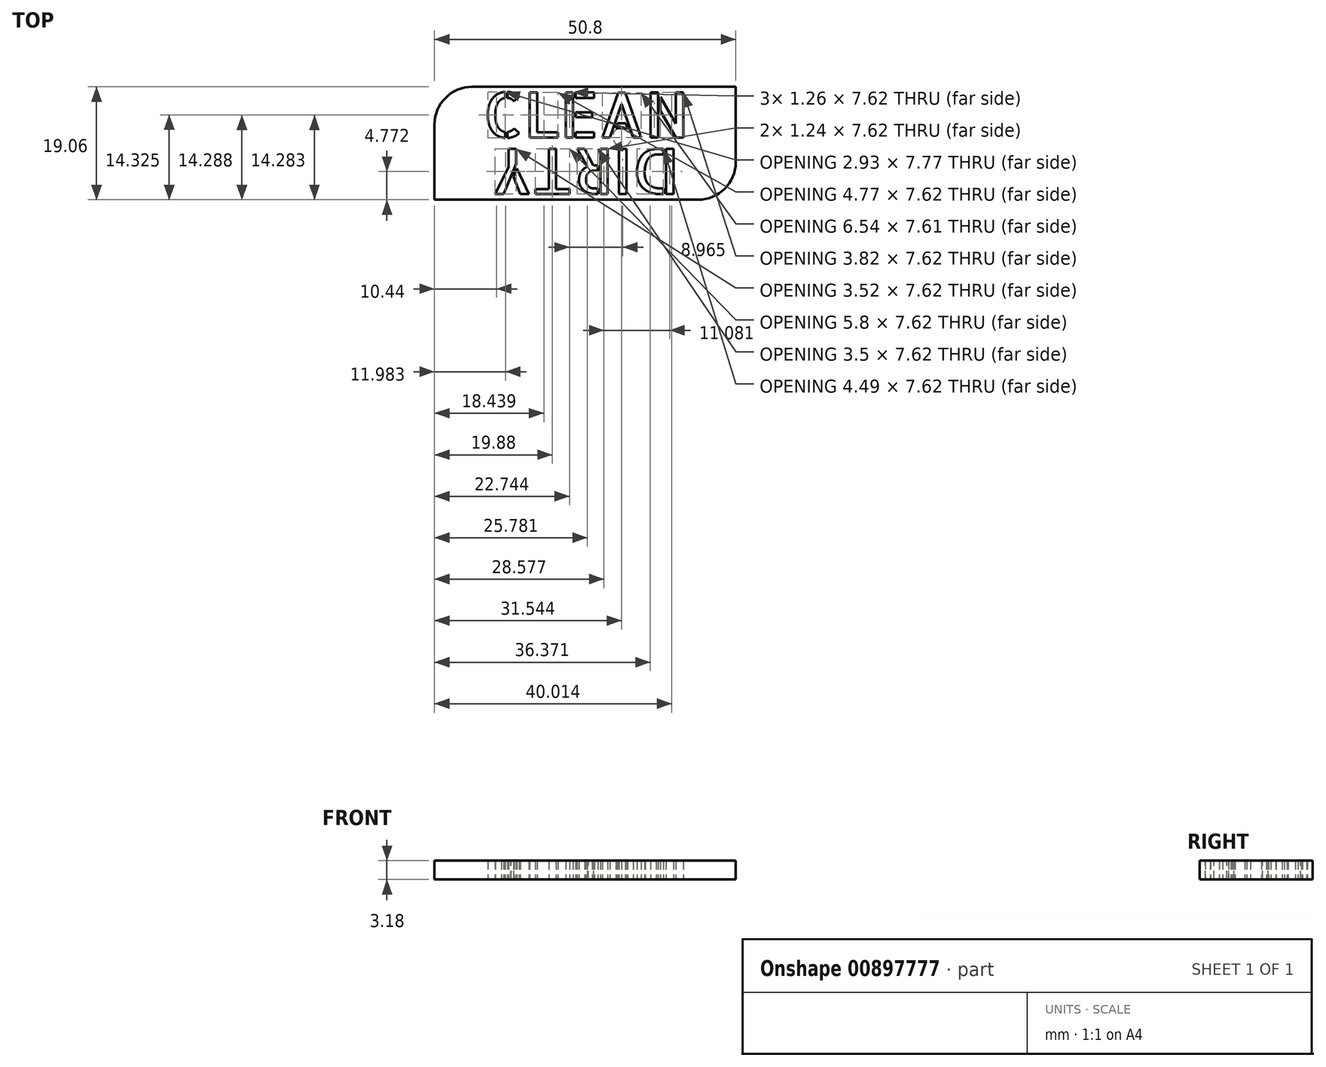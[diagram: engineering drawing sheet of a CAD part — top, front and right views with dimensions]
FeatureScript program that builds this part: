
annotation { "Feature Type Name" : "Feature", "Feature Type Description" : "" }
export const myFeature = defineFeature(function(context is Context, id is Id, definition is map)
    precondition{}
    {
        {
            assignVariable(context, id + "F0", {"name" : "MagnetHeight", "anyValue" : 0.06});
        }
        {
            var Q0;
            Q0=qCreatedBy(makeId("Top.planeOp"),FACE);
            var sketch = newSketch(context, id + "F1", { "sketchPlane" : qUnion([Q0])});
            skLineSegment(sketch, "E0.bottom", {"start": v(-36.28, 9.53) * mm, "end": v(8.17, 9.52) * mm});
            skLineSegment(sketch, "E0.top", {"start": v(-42.63, -9.52) * mm, "end": v(1.82, -9.53) * mm});
            skLineSegment(sketch, "E0.left", {"start": v(-42.63, 3.18) * mm, "end": v(-42.63, -9.52) * mm});
            skLineSegment(sketch, "E0.right", {"start": v(8.17, 9.52) * mm, "end": v(8.17, -3.18) * mm});
            skLineSegment(sketch, "E1", {"start": v(-42.63, 0) * mm, "end": v(8.17, 0) * mm, "construction": true});
            skText(sketch, "E2", { "text": "DIRTY", "fontName": "AllertaStencil-Regular.ttf"});
            skPoint(sketch, "E3.visualSharp", {"position": v(-42.63, 9.52) * mm});
            skArc(sketch, "E3.filletArc", {"start": v(-36.28, 9.53) * mm, "mid": v(-40.77, 7.67) * mm, "end": v(-42.63, 3.18) * mm});
            skPoint(sketch, "E4.visualSharp", {"position": v(8.17, -9.52) * mm});
            skArc(sketch, "E4.filletArc", {"start": v(1.82, -9.53) * mm, "mid": v(6.3, -7.67) * mm, "end": v(8.17, -3.18) * mm});
            skText(sketch, "E5", { "text": "CLEAN", "fontName": "AllertaStencil-Regular.ttf"});
            const initialGuessF1  = {"E2": [-0.00136, -0.00095, -1, 0, 0.00762], "E5": [-0.03447, 0.00095, 1, 0, 0.00762]};
            skSetInitialGuess(sketch, initialGuessF1);
            skSolve(sketch);
        }
        {
            var Q0;
            Q0=makeQuery(id+"F1.imprint","IMPRINT",FACE,{"disambiguationData":[TD([[makeQuery(id+"F1.imprint","IMPRINT",EDGE,{"derivedFrom":sQuery(id+"F1.wireOp",EDGE,"E0.bottom")}),-1.0]])]});
            extrude(context, id + "F2", {"entities" : qUnion([Q0]), "depth" : 3.17 * mm, "offsetDistance" : 25.4 * mm});
        }
        {
            var Q0;
            Q0=makeQuery(id+"F1.imprint","IMPRINT",FACE,{"disambiguationData":[TD([[makeQuery(id+"F1.imprint","IMPRINT",EDGE,{"derivedFrom":sQuery(id+"F1.wireOp",EDGE,"E5.sketch_text.stroke-41")}),1.0]])]});
            var sketch = newSketch(context, id + "F3", { "sketchPlane" : qUnion([Q0])});
            skCircle(sketch, "E6", {"center": v(-10.98, 1.1) * mm, "radius": 1.59 * mm});
            skSolve(sketch);
        }
        {
            var Q0;
            Q0 = qSketchRegion(id + "F3", true);
            extrude(context, id + "F4", {"entities" : qUnion([Q0]), "operationType" : NewBodyOperationType.REMOVE, "oppositeDirection" : true, "depth" : -(getVariable(context, 'MagnetHeight')) * mm, "offsetDistance" : 25.4 * mm});
        }
    });
